# Revit family: FP-Revit18-CPV3-486GD-L-GasRangetop-0-CA-US-90002259A
name_source: partatom
category: Specialty Equipment
revit_build: Autodesk Revit 2018 (Build: 20170223_1515(x64)
units: mm (PartAtom-declared; Revit-internal decimal feet)

## family parameters
Always vertical = Yes
Cut with Voids When Loaded = Yes
OmniClass Number = 23.40.40.14.17.17
OmniClass Title = Ranges
Part Type = Normal
Room Calculation Point = No
Round Connector Dimension = Use Diameter
Shared = No
Work Plane-Based = No

## types (2) — shared parameters
Cavity - Depth = 677 mm  [stored 2.22113 ft]
Cavity - Height = 213 mm  [stored 0.698819 ft]
Cavity - Width = 1219 mm
Chassis - Depth = 677 mm  [stored 2.22113 ft]
Chassis - Height = 213 mm  [stored 0.698819 ft]
Clearance - Overhead Combustible = 914 mm  [stored 2.99869 ft]
Clearance - Overhead Non-Combustible = 762 mm  [stored 2.5 ft]
Clearance - Overhead Rangehood = 914 mm  [stored 2.99869 ft]
Clearance - Rear Combustible = 305 mm  [stored 1.00066 ft]
Clearance - Side Combustible = 305 mm  [stored 1.00066 ft]
Connector Note - Electrical = 120 V, 60Hz, 7 A Max Current
Description = Gas Rangetop, 48", 6 Burners with Griddle
Manufacturer = Fisher & Paykel Appliances
Material - Body = Fisher & Paykel - Stainless Steel
Material - Burner Pan = Fisher & Paykel - Black
Material - Burners & Trivets = Fisher & Paykel - Black, Matte
Material - Trim = Fisher & Paykel - Aluminium
Product - Depth = 728 mm  [stored 2.38845 ft]
Product - Height = 253 mm  [stored 0.830052 ft]
Product - Width = 1216 mm  [stored 3.9895 ft]
URL = www.fisherpaykel.com
Visibility - Clearance Required = Yes

## per-type parameters (varying)
| type | Connector Note - Gas |
| CPV3-486GD-N | NG 6" to 9" WC, with 1/2” NPT Minimum 5/8” dia. flex line |
| CPV3-486GD-L | LPG 11" to 14" WC, with 1/2” NPT Minimum 5/8” dia. flex line |

note: column(s) folded — value = type name in every type: Model

note: [stored X ft] marks values corroborated as IEEE doubles in the binary element streams (Revit-internal decimal feet)

## geometry (parser evidence)
native form markers: Sweep x12
no freeform markers — native parametric forms only
